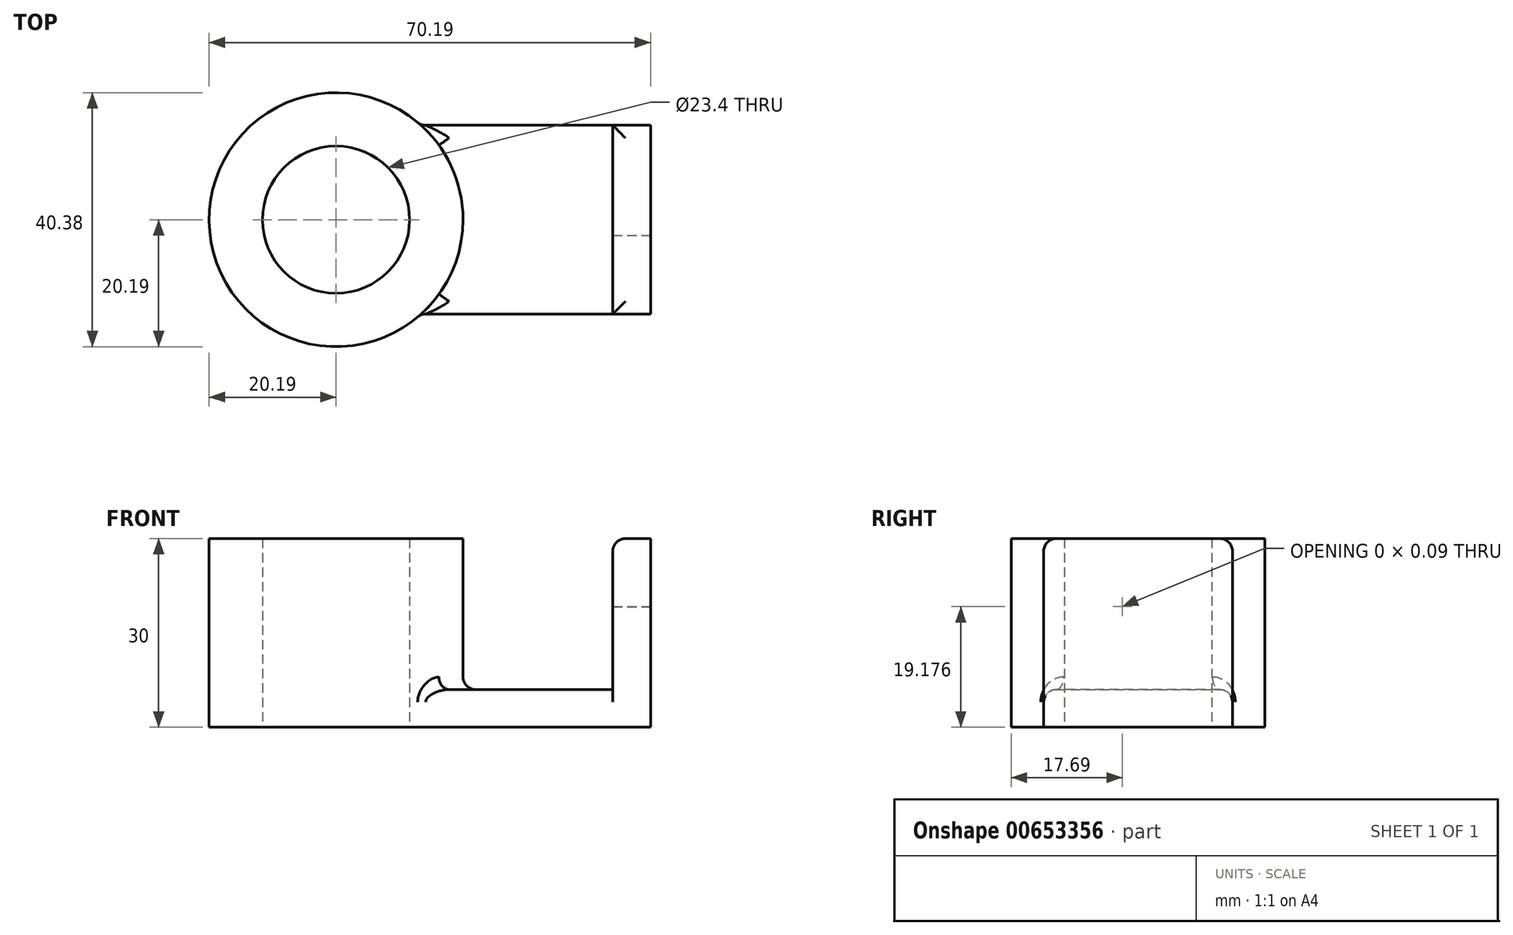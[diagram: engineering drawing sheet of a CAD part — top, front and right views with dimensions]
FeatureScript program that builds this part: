
annotation { "Feature Type Name" : "Feature", "Feature Type Description" : "" }
export const myFeature = defineFeature(function(context is Context, id is Id, definition is map)
    precondition{}
    {
        {
            var Q0;
            Q0=qCreatedBy(makeId("Top.planeOp"),FACE);
            var sketch = newSketch(context, id + "F0", { "sketchPlane" : qUnion([Q0])});
            skCircle(sketch, "E0", {"center": v(0, 0) * mm, "radius": 20.19 * mm});
            skCircle(sketch, "E1", {"center": v(0, 0) * mm, "radius": 11.7 * mm});
            skSolve(sketch);
        }
        {
            var Q0;
            Q0=makeQuery(id+"F0.imprint","IMPRINT",FACE,{"disambiguationData":[TD([[makeQuery(id+"F0.imprint","IMPRINT",EDGE,{"derivedFrom":sQuery(id+"F0.wireOp",EDGE,"E0")}),1.0]])]});
            extrude(context, id + "F1", {"entities" : qUnion([Q0]), "depth" : 30 * mm, "offsetDistance" : 25 * mm});
        }
        {
            var Q0;
            Q0=qCreatedBy(makeId("Top.planeOp"),FACE);
            var sketch = newSketch(context, id + "F2", { "sketchPlane" : qUnion([Q0])});
            skLineSegment(sketch, "E2.bottom", {"start": v(12, 15) * mm, "end": v(50, 15) * mm});
            skLineSegment(sketch, "E2.top", {"start": v(12, -15) * mm, "end": v(50, -15) * mm});
            skLineSegment(sketch, "E2.left", {"start": v(12, 15) * mm, "end": v(12, -15) * mm});
            skLineSegment(sketch, "E2.right", {"start": v(50, 15) * mm, "end": v(50, -15) * mm});
            skSolve(sketch);
        }
        {
            var Q0;
            Q0 = qSketchRegion(id + "F2", true);
            extrude(context, id + "F3", {"entities" : qUnion([Q0]), "operationType" : NewBodyOperationType.ADD, "depth" : 6 * mm, "offsetDistance" : 25 * mm});
        }
        {
            var Q0;
            Q0=makeQuery(id+"F3.opExtrude","SWEPT_FACE",FACE,{"disambiguationData":[OSD([sQuery(id+"F2.wireOp",EDGE,"E2.right")])]});
            var sketch = newSketch(context, id + "F4", { "sketchPlane" : qUnion([Q0])});
            skLineSegment(sketch, "E3.bottom", {"start": v(-15, 6) * mm, "end": v(15, 6) * mm});
            skLineSegment(sketch, "E3.top", {"start": v(-15, 30) * mm, "end": v(15, 30) * mm});
            skLineSegment(sketch, "E3.left", {"start": v(-15, 6) * mm, "end": v(-15, 30) * mm});
            skLineSegment(sketch, "E3.right", {"start": v(15, 6) * mm, "end": v(15, 30) * mm});
            skSolve(sketch);
        }
        {
            var Q0;
            Q0=makeQuery(id+"F4.imprint","IMPRINT",FACE,{"disambiguationData":[TD([[makeQuery(id+"F4.imprint","IMPRINT",EDGE,{"derivedFrom":sQuery(id+"F4.wireOp",EDGE,"E3.bottom")}),-1.0]])]});
            extrude(context, id + "F5", {"entities" : qUnion([Q0]), "operationType" : NewBodyOperationType.ADD, "oppositeDirection" : true, "depth" : 6 * mm, "offsetDistance" : 25 * mm});
        }
        {
            var Q0;
            Q0=makeQuery(id+"F5.boolean.opBoolean","MERGE",FACE,{"derivedFrom":[makeQuery(id+"F3.opExtrude","SWEPT_FACE",FACE,{"disambiguationData":[OSD([sQuery(id+"F2.wireOp",EDGE,"E2.right")])]}),makeQuery(id+"F5.opExtrude","CAP_FACE",FACE,{"disambiguationData":[OSD([sQuery(id+"F4.wireOp",EDGE,"E3.bottom"),sQuery(id+"F4.wireOp",EDGE,"E3.top"),sQuery(id+"F4.wireOp",EDGE,"E3.left"),sQuery(id+"F4.wireOp",EDGE,"E3.right")])],"isStart":true})]});
            var sketch = newSketch(context, id + "F6", { "sketchPlane" : qUnion([Q0])});
            skLineSegment(sketch, "E4", {"start": v(0, 30) * mm, "end": v(0, 0) * mm, "construction": true});
            skArc(sketch, "E5", {"start": v(-2.5, 19.22) * mm, "mid": v(0.07, 16.68) * mm, "end": v(2.5, 19.36) * mm});
            skLineSegment(sketch, "E6", {"start": v(-2.5, 19.13) * mm, "end": v(-2.5, 30) * mm});
            skLineSegment(sketch, "E7", {"start": v(2.5, 19.36) * mm, "end": v(2.5, 30) * mm});
            skSolve(sketch);
        }
        {
            var Q0;
            {var subQ5=sQuery(id+"F6.wireOp",EDGE,"E5");Q0=makeQuery(id+"F6.imprint","IMPRINT",FACE,{"disambiguationData":[TD([[makeQuery(id+"F6.imprint","IMPRINT",EDGE,{"derivedFrom":subQ5}),1.0]])]});}
            var Q1;
            Q1=makeQuery(id+"F5.opExtrude","CAP_FACE",FACE,{"disambiguationData":[OSD([sQuery(id+"F4.wireOp",EDGE,"E3.bottom"),sQuery(id+"F4.wireOp",EDGE,"E3.top"),sQuery(id+"F4.wireOp",EDGE,"E3.left"),sQuery(id+"F4.wireOp",EDGE,"E3.right")])],"isStart":false});
            extrude(context, id + "F7", {"entities" : qUnion([Q0, Q1]), "operationType" : NewBodyOperationType.REMOVE, "oppositeDirection" : true, "depth" : 10 * mm, "offsetDistance" : 25 * mm});
        }
        {
            var Q0;
            Q0=makeQuery(id+"F3.boolean.opBoolean","INTERSECT",EDGE,{"derivedFrom":[makeQuery(id+"F1.opExtrude","SWEPT_FACE",FACE,{"disambiguationData":[OSD([sQuery(id+"F0.wireOp",EDGE,"E0")])]}),makeQuery(id+"F3.opExtrude","CAP_FACE",FACE,{"disambiguationData":[OSD([sQuery(id+"F2.wireOp",EDGE,"E2.bottom"),sQuery(id+"F2.wireOp",EDGE,"E2.top"),sQuery(id+"F2.wireOp",EDGE,"E2.left"),sQuery(id+"F2.wireOp",EDGE,"E2.right")])],"isStart":false})]});
            var Q1;
            Q1=makeQuery(id+"F3.boolean.opBoolean","INTERSECT",EDGE,{"derivedFrom":[makeQuery(id+"F1.opExtrude","SWEPT_FACE",FACE,{"disambiguationData":[OSD([sQuery(id+"F0.wireOp",EDGE,"E0")])]}),makeQuery(id+"F3.opExtrude","SWEPT_FACE",FACE,{"disambiguationData":[OSD([sQuery(id+"F2.wireOp",EDGE,"E2.top")])]})]});
            var Q2;
            Q2=makeQuery(id+"F3.opExtrude","CAP_EDGE",EDGE,{"disambiguationData":[OSD([sQuery(id+"F2.wireOp",EDGE,"E2.top")])],"isStart":false});
            var Q3;
            Q3=makeQuery(id+"F5.opExtrude","CAP_EDGE",EDGE,{"disambiguationData":[OSD([sQuery(id+"F4.wireOp",EDGE,"E3.bottom")])],"isStart":false});
            var Q4;
            Q4=makeQuery(id+"F5.opExtrude","SWEPT_EDGE",EDGE,{"disambiguationData":[OSD([sQuery(id+"F4.wireOp",EDGE,"E3.top"),sQuery(id+"F4.wireOp",EDGE,"E3.left")])]});
            var Q5;
            {var subQ0=sQuery(id+"F4.wireOp",EDGE,"E3.top");Q5=makeQuery(id+"F7.boolean.opBoolean","SPLIT",EDGE,{"disambiguationData":[TD([makeQuery(id+"F3.opExtrude","SWEPT_FACE",FACE,{"disambiguationData":[OSD([sQuery(id+"F2.wireOp",EDGE,"E2.top")])]})])],"derivedFrom":makeQuery(id+"F5.opExtrude","CAP_EDGE",EDGE,{"disambiguationData":[OSD([subQ0])],"isStart":false})});}
            var Q6;
            Q6=makeQuery(id+"F3.boolean.opBoolean","INTERSECT",EDGE,{"derivedFrom":[makeQuery(id+"F1.opExtrude","SWEPT_FACE",FACE,{"disambiguationData":[OSD([sQuery(id+"F0.wireOp",EDGE,"E0")])]}),makeQuery(id+"F3.opExtrude","SWEPT_FACE",FACE,{"disambiguationData":[OSD([sQuery(id+"F2.wireOp",EDGE,"E2.bottom")])]})]});
            var Q7;
            Q7=makeQuery(id+"F3.opExtrude","CAP_EDGE",EDGE,{"disambiguationData":[OSD([sQuery(id+"F2.wireOp",EDGE,"E2.bottom")])],"isStart":false});
            var Q8;
            {var subQ1=sQuery(id+"F4.wireOp",EDGE,"E3.top");Q8=makeQuery(id+"F7.boolean.opBoolean","SPLIT",EDGE,{"disambiguationData":[TD([makeQuery(id+"F3.opExtrude","SWEPT_FACE",FACE,{"disambiguationData":[OSD([sQuery(id+"F2.wireOp",EDGE,"E2.bottom")])]})])],"derivedFrom":makeQuery(id+"F5.opExtrude","CAP_EDGE",EDGE,{"disambiguationData":[OSD([subQ1])],"isStart":false})});}
            var Q9;
            Q9=makeQuery(id+"F5.opExtrude","SWEPT_EDGE",EDGE,{"disambiguationData":[OSD([sQuery(id+"F4.wireOp",EDGE,"E3.top"),sQuery(id+"F4.wireOp",EDGE,"E3.right")])]});
            fillet(context, id + "F8", {"entities" : qUnion([Q0, Q1, Q2, Q3, Q4, Q5, Q6, Q7, Q8, Q9]), "radius" : 2 * mm, "tangentPropagation" : true, "allowEdgeOverflow" : false});
        }
    });
